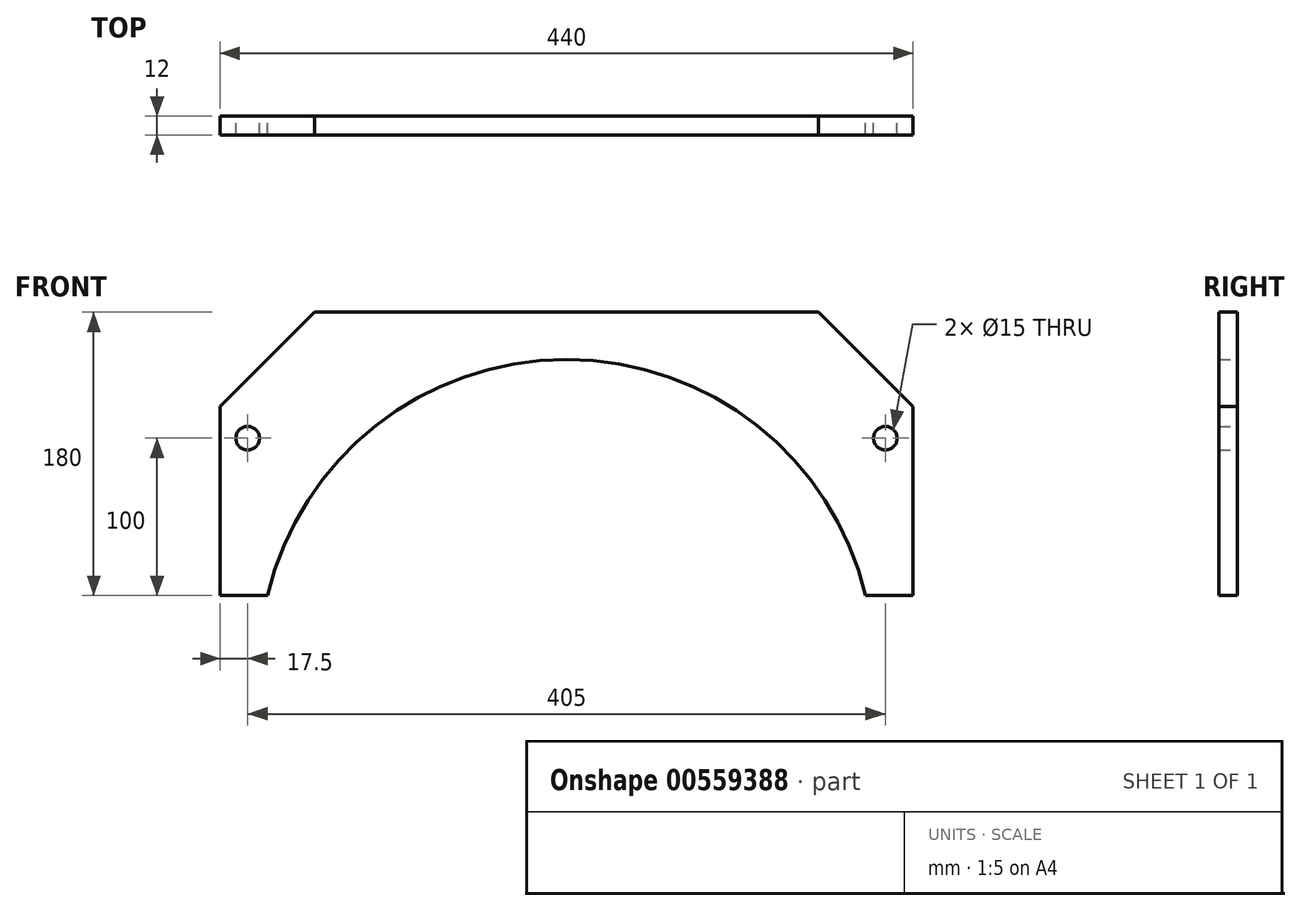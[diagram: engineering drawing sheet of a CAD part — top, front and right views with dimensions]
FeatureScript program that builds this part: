
annotation { "Feature Type Name" : "Feature", "Feature Type Description" : "" }
export const myFeature = defineFeature(function(context is Context, id is Id, definition is map)
    precondition{}
    {
        {
            var Q0;
            Q0=qCreatedBy(makeId("Front.planeOp"),FACE);
            var sketch = newSketch(context, id + "F0", { "sketchPlane" : qUnion([Q0])});
            skArc(sketch, "E0", {"start": v(380, 0) * mm, "mid": v(190, 150.03) * mm, "end": v(0, 0) * mm});
            skLineSegment(sketch, "E1", {"start": v(0, 0) * mm, "end": v(-30, 0) * mm});
            skLineSegment(sketch, "E2", {"start": v(-30, 0) * mm, "end": v(-30, 180) * mm});
            skLineSegment(sketch, "E3", {"start": v(-30, 180) * mm, "end": v(410, 180) * mm});
            skLineSegment(sketch, "E4", {"start": v(410, 180) * mm, "end": v(410, 0) * mm});
            skLineSegment(sketch, "E5", {"start": v(410, 0) * mm, "end": v(380, 0) * mm});
            skLineSegment(sketch, "E6", {"start": v(-30, 120) * mm, "end": v(30, 180) * mm});
            skLineSegment(sketch, "E7", {"start": v(350, 180) * mm, "end": v(410, 120) * mm});
            skCircle(sketch, "E8", {"center": v(-12.5, 100) * mm, "radius": 7.5 * mm});
            skCircle(sketch, "E9", {"center": v(392.5, 100) * mm, "radius": 7.5 * mm});
            skSolve(sketch);
        }
        {
            var Q0;
            Q0=makeQuery(id+"F0.imprint","IMPRINT",FACE,{"disambiguationData":[TD([[makeQuery(id+"F0.imprint","IMPRINT",EDGE,{"derivedFrom":sQuery(id+"F0.wireOp",EDGE,"E0")}),-1.0]])]});
            extrude(context, id + "F1", {"entities" : qUnion([Q0]), "depth" : 12 * mm, "offsetDistance" : 25 * mm});
        }
    });
